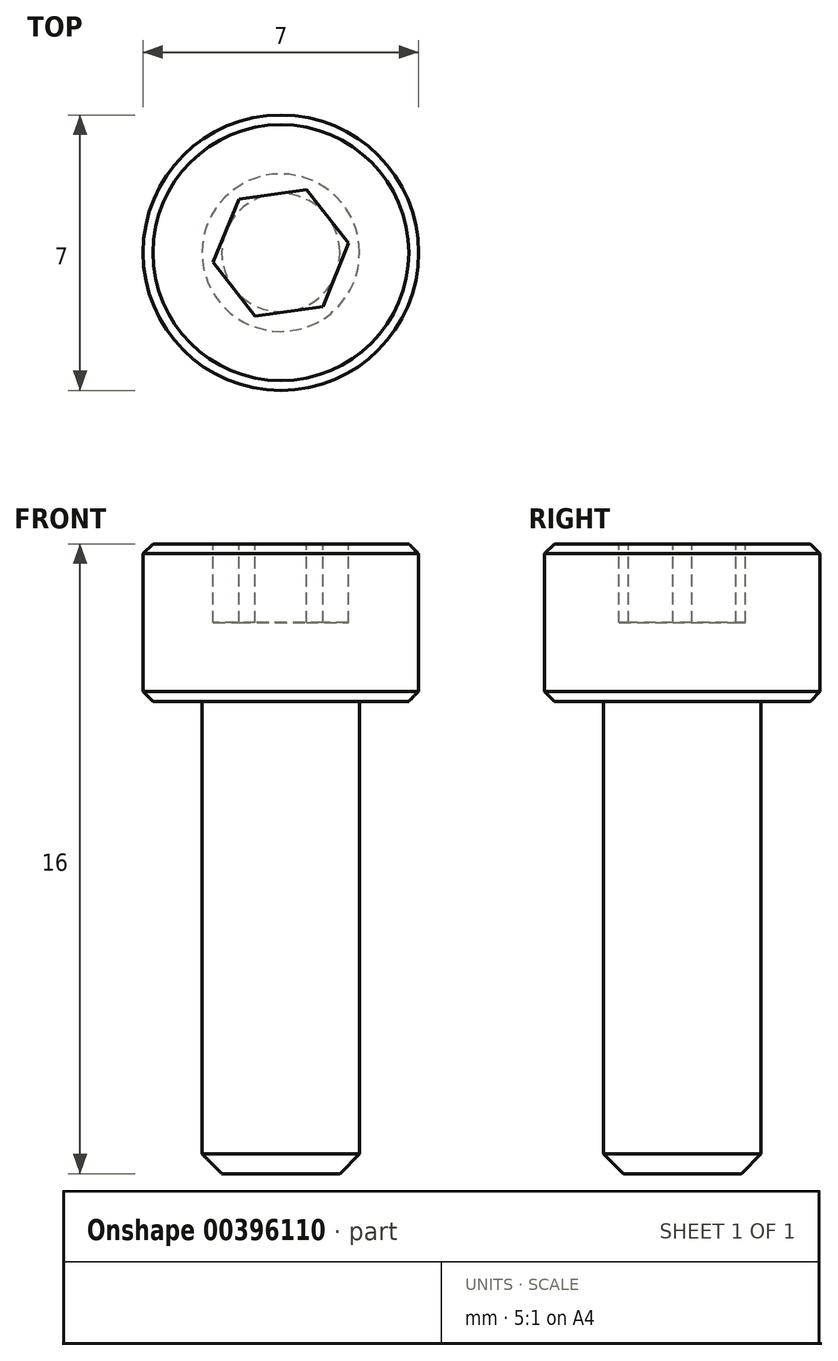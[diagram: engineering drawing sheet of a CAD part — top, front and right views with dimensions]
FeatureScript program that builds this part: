
annotation { "Feature Type Name" : "Feature", "Feature Type Description" : "" }
export const myFeature = defineFeature(function(context is Context, id is Id, definition is map)
    precondition{}
    {
        {
            var Q0;
            Q0=qCreatedBy(makeId("Top.planeOp"),FACE);
            var sketch = newSketch(context, id + "F0", { "sketchPlane" : qUnion([Q0])});
            skCircle(sketch, "E0", {"center": v(0, 0) * mm, "radius": 3.5 * mm});
            skSolve(sketch);
        }
        {
            var Q0;
            Q0=qSketchRegion(id+"F0",true);
            extrude(context, id + "F1", {"entities" : qUnion([Q0]), "depth" : 4 * mm});
        }
        {
            var Q0;
            Q0=makeQuery(id+"F1.opExtrude","CAP_FACE",FACE,{"disambiguationData":[OSD([sQuery(id+"F0.wireOp",EDGE,"E0")])],"isStart":false});
            var sketch = newSketch(context, id + "F2", { "sketchPlane" : qUnion([Q0])});
            skCircle(sketch, "E1.cCircle", {"center": v(0, 0) * mm, "radius": 1.5 * mm, "construction": true});
            skLineSegment(sketch, "E1.0", {"start": v(1.72, 0.24) * mm, "end": v(1.07, -1.37) * mm});
            skLineSegment(sketch, "E1.1", {"start": v(1.07, -1.37) * mm, "end": v(-0.65, -1.6) * mm});
            skLineSegment(sketch, "E1.2", {"start": v(-0.65, -1.6) * mm, "end": v(-1.72, -0.24) * mm});
            skLineSegment(sketch, "E1.3", {"start": v(-1.72, -0.24) * mm, "end": v(-1.07, 1.37) * mm});
            skLineSegment(sketch, "E1.4", {"start": v(-1.07, 1.37) * mm, "end": v(0.65, 1.6) * mm});
            skLineSegment(sketch, "E1.5", {"start": v(0.65, 1.6) * mm, "end": v(1.72, 0.24) * mm});
            skPoint(sketch, "E1.0.midPoint", {"position": v(1.4, -0.56) * mm});
            skSolve(sketch);
        }
        {
            var Q0;
            Q0=qSketchRegion(id+"F2",true);
            extrude(context, id + "F3", {"entities" : qUnion([Q0]), "operationType" : NewBodyOperationType.REMOVE, "oppositeDirection" : true, "depth" : 2 * mm});
        }
        {
            var Q0;
            Q0=makeQuery(id+"F1.opExtrude","CAP_FACE",FACE,{"disambiguationData":[OSD([sQuery(id+"F0.wireOp",EDGE,"E0")])],"isStart":true});
            var sketch = newSketch(context, id + "F4", { "sketchPlane" : qUnion([Q0])});
            skCircle(sketch, "E2", {"center": v(0, 0) * mm, "radius": 2 * mm});
            skSolve(sketch);
        }
        {
            var Q0;
            Q0=qSketchRegion(id+"F4",true);
            extrude(context, id + "F5", {"entities" : qUnion([Q0]), "depth" : 12 * mm});
        }
        {
            var Q0;
            Q0=makeQuery(id+"F5.opExtrude","CAP_EDGE",EDGE,{"disambiguationData":[OSD([sQuery(id+"F4.wireOp",EDGE,"E2")])],"isStart":false});
            chamfer(context, id + "F6", {"entities" : qUnion([Q0]), "width" : .5 * mm, "tangentPropagation" : true});
        }
        {
            var Q0;
            Q0=makeQuery(id+"F1.opExtrude","CAP_EDGE",EDGE,{"disambiguationData":[OSD([sQuery(id+"F0.wireOp",EDGE,"E0")])],"isStart":true});
            var Q1;
            Q1=makeQuery(id+"F1.opExtrude","CAP_EDGE",EDGE,{"disambiguationData":[OSD([sQuery(id+"F0.wireOp",EDGE,"E0")])],"isStart":false});
            chamfer(context, id + "F7", {"entities" : qUnion([Q0, Q1]), "width" : .25 * mm, "tangentPropagation" : true});
        }
    });
